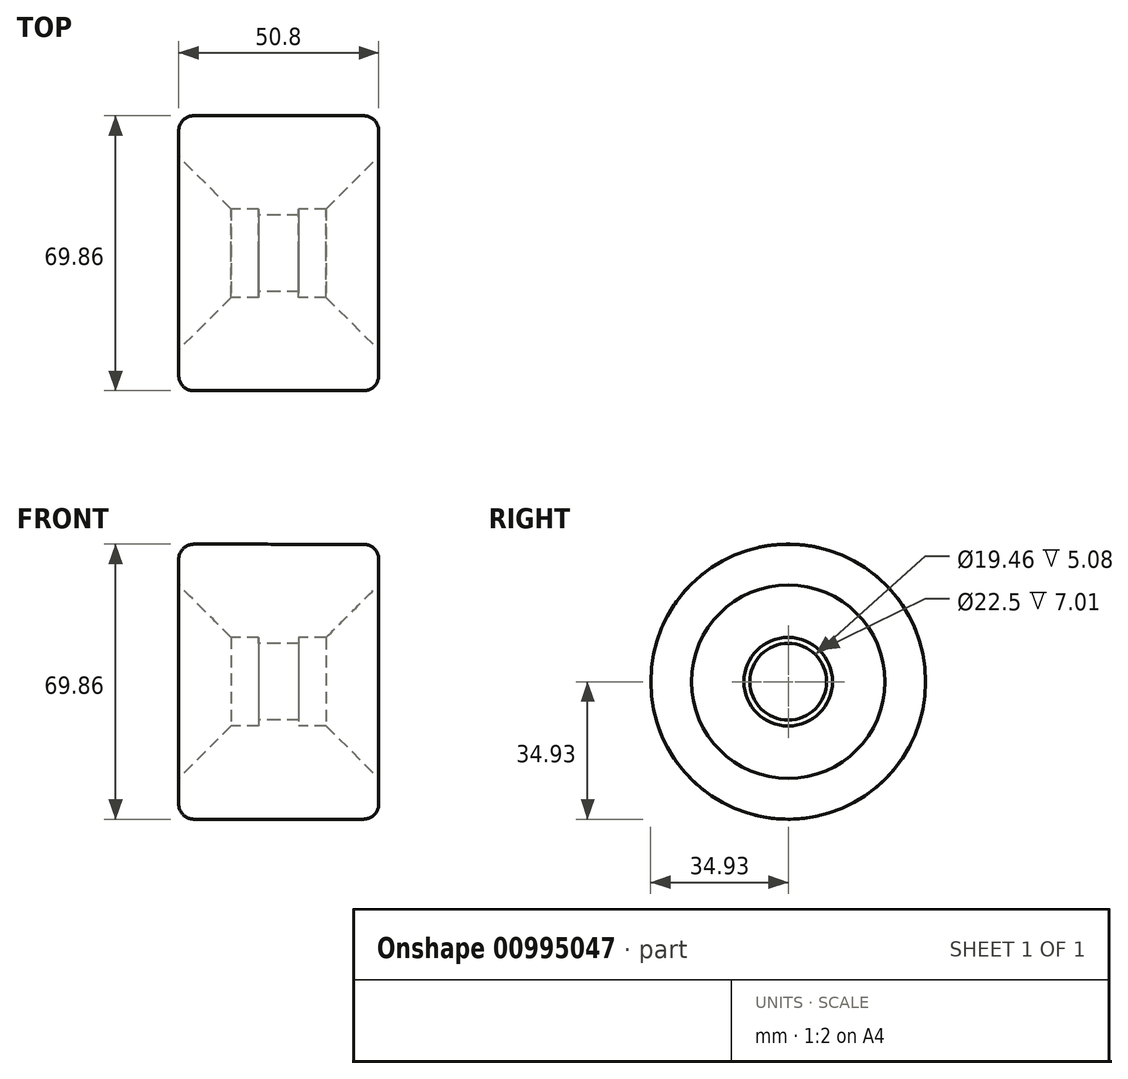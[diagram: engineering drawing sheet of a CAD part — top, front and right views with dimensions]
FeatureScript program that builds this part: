
annotation { "Feature Type Name" : "Feature", "Feature Type Description" : "" }
export const myFeature = defineFeature(function(context is Context, id is Id, definition is map)
    precondition{}
    {
        {
            var Q0;
            Q0=qCreatedBy(makeId("Front.planeOp"),FACE);
            var sketch = newSketch(context, id + "F0", { "sketchPlane" : qUnion([Q0])});
            skLineSegment(sketch, "E0", {"start": v(-46.4, 0) * mm, "end": v(57.18, 0) * mm, "construction": true});
            skLineSegment(sketch, "E1", {"start": v(0, 34.92) * mm, "end": v(25.4, 34.92) * mm});
            skLineSegment(sketch, "E2", {"start": v(25.4, 34.92) * mm, "end": v(25.4, 24.57) * mm});
            skLineSegment(sketch, "E3", {"start": v(25.4, 24.57) * mm, "end": v(12.1, 11.25) * mm});
            skLineSegment(sketch, "E4", {"start": v(12.1, 11.25) * mm, "end": v(5.08, 11.25) * mm});
            skLineSegment(sketch, "E5", {"start": v(5.08, 11.25) * mm, "end": v(5.08, 9.73) * mm});
            skLineSegment(sketch, "E6", {"start": v(5.08, 9.73) * mm, "end": v(0, 9.73) * mm});
            skLineSegment(sketch, "E7", {"start": v(0, 9.73) * mm, "end": v(0, 34.92) * mm});
            skLineSegment(sketch, "E8.MirrorCS", {"start": v(-25.4, 34.93) * mm, "end": v(-25.4, 24.57) * mm});
            skLineSegment(sketch, "E9.MirrorCS", {"start": v(25.4, 34.93) * mm, "end": v(25.4, 24.57) * mm});
            skLineSegment(sketch, "E10.MirrorCS", {"start": v(-25.4, 24.57) * mm, "end": v(-12.09, 11.26) * mm});
            skLineSegment(sketch, "E11.MirrorCS", {"start": v(0, 34.93) * mm, "end": v(-25.4, 34.93) * mm});
            skLineSegment(sketch, "E12.MirrorCS", {"start": v(-12.09, 11.26) * mm, "end": v(-5.08, 11.25) * mm});
            skLineSegment(sketch, "E13.MirrorCS", {"start": v(-5.08, 9.73) * mm, "end": v(0, 9.73) * mm});
            skLineSegment(sketch, "E14.MirrorCS", {"start": v(-5.08, 11.25) * mm, "end": v(-5.08, 9.73) * mm});
            skSolve(sketch);
        }
        {
            var Q0;
            Q0=makeQuery(id+"F0.imprint","IMPRINT",FACE,{"disambiguationData":[TD([[makeQuery(id+"F0.imprint","IMPRINT",EDGE,{"derivedFrom":sQuery(id+"F0.wireOp",EDGE,"E7")}),1.0]])]});
            var Q1;
            Q1=makeQuery(id+"F0.imprint","IMPRINT",FACE,{"disambiguationData":[TD([[makeQuery(id+"F0.imprint","IMPRINT",EDGE,{"derivedFrom":sQuery(id+"F0.wireOp",EDGE,"E1")}),-1.0]])]});
            var Q2;
            Q2=sQuery(id+"F0.wireOp",EDGE,"E0");
            revolve(context, id + "F1", {"surfaceOperationType" : NewSurfaceOperationType.NEW, "entities" : qUnion([Q0, Q1]), "axis" : qUnion([Q2]), "revolveType" : RevolveType.FULL});
        }
        {
            var Q0;
            Q0=makeQuery(id+"F1.opRevolve","SWEPT_EDGE",EDGE,{"disambiguationData":[OSD([sQuery(id+"F0.wireOp",EDGE,"E1"),sQuery(id+"F0.wireOp",EDGE,"E9.MirrorCS")])]});
            var Q1;
            Q1=makeQuery(id+"F1.opRevolve","SWEPT_EDGE",EDGE,{"disambiguationData":[OSD([sQuery(id+"F0.wireOp",EDGE,"E8.MirrorCS"),sQuery(id+"F0.wireOp",EDGE,"E11.MirrorCS")])]});
            fillet(context, id + "F2", {"entities" : qUnion([Q0, Q1]), "tangentPropagation" : true, "radius" : 3.8 * mm, "defaultsChanged" : false, "vertexSettings" : [], "allowEdgeOverflow" : false});
        }
    });
